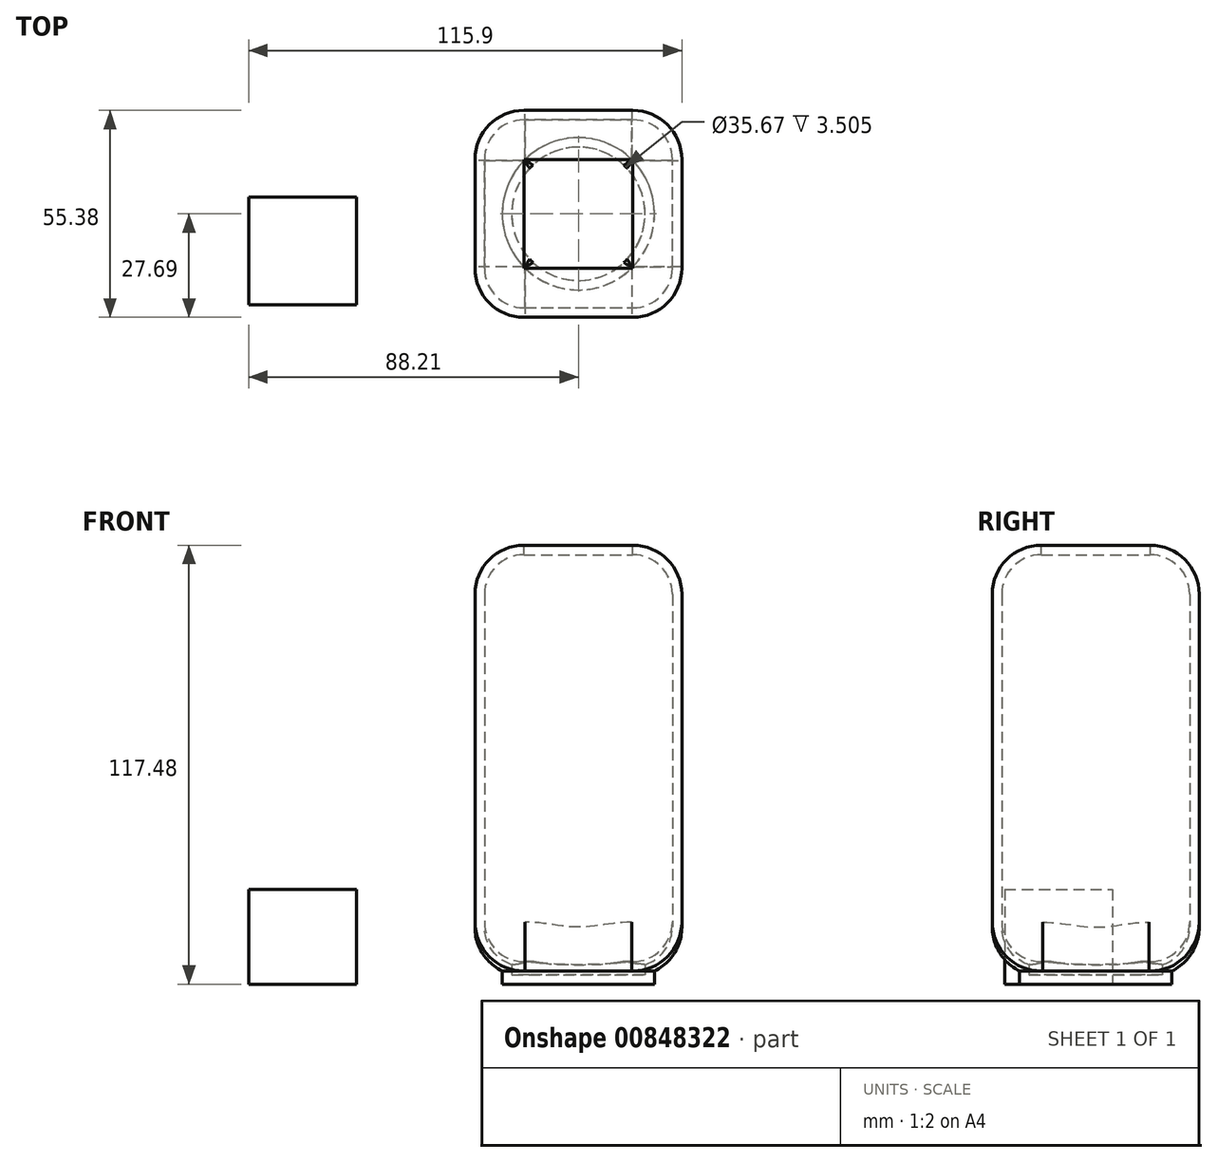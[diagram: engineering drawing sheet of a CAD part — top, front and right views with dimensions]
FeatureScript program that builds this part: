
annotation { "Feature Type Name" : "Feature", "Feature Type Description" : "" }
export const myFeature = defineFeature(function(context is Context, id is Id, definition is map)
    precondition{}
    {
        {
            var Q0;
            Q0=qCreatedBy(makeId("Top.planeOp"),FACE);
            var sketch = newSketch(context, id + "F0", { "sketchPlane" : qUnion([Q0])});
            skCircle(sketch, "E0", {"center": v(0, 0) * mm, "radius": 20.38 * mm});
            skSolve(sketch);
        }
        {
            var Q0;
            Q0=makeQuery(id+"F0.imprint","IMPRINT",FACE,{"disambiguationData":[TD([[makeQuery(id+"F0.imprint","IMPRINT",EDGE,{"derivedFrom":sQuery(id+"F0.wireOp",EDGE,"E0")}),1.0]])]});
            extrude(context, id + "F1", {"entities" : qUnion([Q0]), "depth" : 3.5 * mm, "offsetDistance" : 25.4 * mm});
        }
        {
            var Q0;
            Q0=makeQuery(id+"F1.opExtrude","CAP_FACE",FACE,{"disambiguationData":[OSD([sQuery(id+"F0.wireOp",EDGE,"E0")])],"isStart":false});
            var sketch = newSketch(context, id + "F2", { "sketchPlane" : qUnion([Q0])});
            skLineSegment(sketch, "E1.bottom", {"start": v(27.69, 27.69) * mm, "end": v(-27.69, 27.69) * mm});
            skLineSegment(sketch, "E1.top", {"start": v(27.69, -27.69) * mm, "end": v(-27.69, -27.69) * mm});
            skLineSegment(sketch, "E1.left", {"start": v(27.69, 27.69) * mm, "end": v(27.69, -27.69) * mm});
            skLineSegment(sketch, "E1.right", {"start": v(-27.69, 27.69) * mm, "end": v(-27.69, -27.69) * mm});
            skPoint(sketch, "E1.middle", {"position": v(0, 0) * mm});
            skSolve(sketch);
        }
        {
            var Q0;
            Q0 = qSketchRegion(id + "F2", true);
            extrude(context, id + "F3", {"entities" : qUnion([Q0]), "operationType" : NewBodyOperationType.ADD, "depth" : 113.97 * mm, "offsetDistance" : 25.4 * mm});
        }
        {
            var Q0;
            Q0=makeQuery(id+"F3.opExtrude","SWEPT_EDGE",EDGE,{"disambiguationData":[OSD([sQuery(id+"F2.wireOp",EDGE,"E1.top"),sQuery(id+"F2.wireOp",EDGE,"E1.right")])]});
            var Q1;
            Q1=makeQuery(id+"F3.opExtrude","SWEPT_EDGE",EDGE,{"disambiguationData":[OSD([sQuery(id+"F2.wireOp",EDGE,"E1.top"),sQuery(id+"F2.wireOp",EDGE,"E1.left")])]});
            var Q2;
            Q2=makeQuery(id+"F3.opExtrude","CAP_EDGE",EDGE,{"disambiguationData":[OSD([sQuery(id+"F2.wireOp",EDGE,"E1.top")])],"isStart":false});
            var Q3;
            Q3=makeQuery(id+"F3.opExtrude","CAP_EDGE",EDGE,{"disambiguationData":[OSD([sQuery(id+"F2.wireOp",EDGE,"E1.right")])],"isStart":false});
            var Q4;
            Q4=makeQuery(id+"F3.opExtrude","CAP_EDGE",EDGE,{"disambiguationData":[OSD([sQuery(id+"F2.wireOp",EDGE,"E1.bottom")])],"isStart":false});
            var Q5;
            Q5=makeQuery(id+"F3.opExtrude","SWEPT_EDGE",EDGE,{"disambiguationData":[OSD([sQuery(id+"F2.wireOp",EDGE,"E1.bottom"),sQuery(id+"F2.wireOp",EDGE,"E1.left")])]});
            var Q6;
            Q6=makeQuery(id+"F3.opExtrude","CAP_EDGE",EDGE,{"disambiguationData":[OSD([sQuery(id+"F2.wireOp",EDGE,"E1.left")])],"isStart":false});
            var Q7;
            Q7=makeQuery(id+"F3.opExtrude","CAP_EDGE",EDGE,{"disambiguationData":[OSD([sQuery(id+"F2.wireOp",EDGE,"E1.left")])],"isStart":true});
            var Q8;
            Q8=makeQuery(id+"F3.opExtrude","CAP_EDGE",EDGE,{"disambiguationData":[OSD([sQuery(id+"F2.wireOp",EDGE,"E1.top")])],"isStart":true});
            var Q9;
            Q9=makeQuery(id+"F3.opExtrude","CAP_EDGE",EDGE,{"disambiguationData":[OSD([sQuery(id+"F2.wireOp",EDGE,"E1.bottom")])],"isStart":true});
            var Q10;
            Q10=makeQuery(id+"F3.opExtrude","SWEPT_FACE",FACE,{"disambiguationData":[OSD([sQuery(id+"F2.wireOp",EDGE,"E1.bottom")])]});
            var Q11;
            Q11=makeQuery(id+"F3.opExtrude","SWEPT_FACE",FACE,{"disambiguationData":[OSD([sQuery(id+"F2.wireOp",EDGE,"E1.top")])]});
            var Q12;
            Q12=makeQuery(id+"F3.opExtrude","CAP_EDGE",EDGE,{"disambiguationData":[OSD([sQuery(id+"F2.wireOp",EDGE,"E1.right")])],"isStart":true});
            fillet(context, id + "F4", {"entities" : qUnion([Q0, Q1, Q2, Q3, Q4, Q5, Q6, Q7, Q8, Q9, Q10, Q11, Q12]), "radius" : 13.12 * mm, "tangentPropagation" : true, "allowEdgeOverflow" : false});
        }
        {
            var Q0;
            Q0=makeQuery(id+"F3.opExtrude","CAP_FACE",FACE,{"disambiguationData":[OSD([sQuery(id+"F2.wireOp",EDGE,"E1.bottom"),sQuery(id+"F2.wireOp",EDGE,"E1.top"),sQuery(id+"F2.wireOp",EDGE,"E1.left"),sQuery(id+"F2.wireOp",EDGE,"E1.right")])],"isStart":false});
            var sketch = newSketch(context, id + "F5", { "sketchPlane" : qUnion([Q0])});
            skSolve(sketch);
        }
        {
            var Q0;
            Q0=makeQuery(id+"F3.opExtrude","CAP_FACE",FACE,{"disambiguationData":[OSD([sQuery(id+"F2.wireOp",EDGE,"E1.bottom"),sQuery(id+"F2.wireOp",EDGE,"E1.top"),sQuery(id+"F2.wireOp",EDGE,"E1.left"),sQuery(id+"F2.wireOp",EDGE,"E1.right")])],"isStart":false});
            var Q1;
            Q1=makeQuery(id+"F1.opExtrude","SWEPT_BODY",BODY,{"disambiguationData":[OSD([sQuery(id+"F0.wireOp",EDGE,"E0")])]});
            shell(context, id + "F6", {"entities" : qUnion([Q0]), "parts" : qUnion([Q1]), "thickness" : 2.54 * mm});
        }
        {
            var Q0;
            Q0=qCreatedBy(makeId("Top.planeOp"),FACE);
            var sketch = newSketch(context, id + "F7", { "sketchPlane" : qUnion([Q0])});
            skLineSegment(sketch, "E2.bottom", {"start": v(14.43, 14.43) * mm, "end": v(-14.43, 14.43) * mm});
            skLineSegment(sketch, "E2.top", {"start": v(14.43, -14.43) * mm, "end": v(-14.43, -14.43) * mm});
            skLineSegment(sketch, "E2.left", {"start": v(14.43, 14.43) * mm, "end": v(14.43, -14.43) * mm});
            skLineSegment(sketch, "E2.right", {"start": v(-14.43, 14.43) * mm, "end": v(-14.43, -14.43) * mm});
            skPoint(sketch, "E2.middle", {"position": v(0, 0) * mm});
            skLineSegment(sketch, "E3.bottom", {"start": v(-59.33, -24.4) * mm, "end": v(-88.2, -24.4) * mm});
            skLineSegment(sketch, "E3.top", {"start": v(-59.33, 4.49) * mm, "end": v(-88.2, 4.49) * mm});
            skLineSegment(sketch, "E3.left", {"start": v(-59.33, -24.4) * mm, "end": v(-59.33, 4.49) * mm});
            skLineSegment(sketch, "E3.right", {"start": v(-88.2, -24.4) * mm, "end": v(-88.2, 4.49) * mm});
            skPoint(sketch, "E3.middle", {"position": v(-73.77, -9.95) * mm});
            skSolve(sketch);
        }
        {
            var Q0;
            Q0=makeQuery(id+"F7.imprint","IMPRINT",FACE,{"disambiguationData":[TD([[makeQuery(id+"F7.imprint","IMPRINT",EDGE,{"derivedFrom":sQuery(id+"F7.wireOp",EDGE,"E3.bottom")}),-1.0]])]});
            extrude(context, id + "F8", {"entities" : qUnion([Q0]), "depth" : 25.4 * mm, "offsetDistance" : 25.4 * mm});
        }
    });
